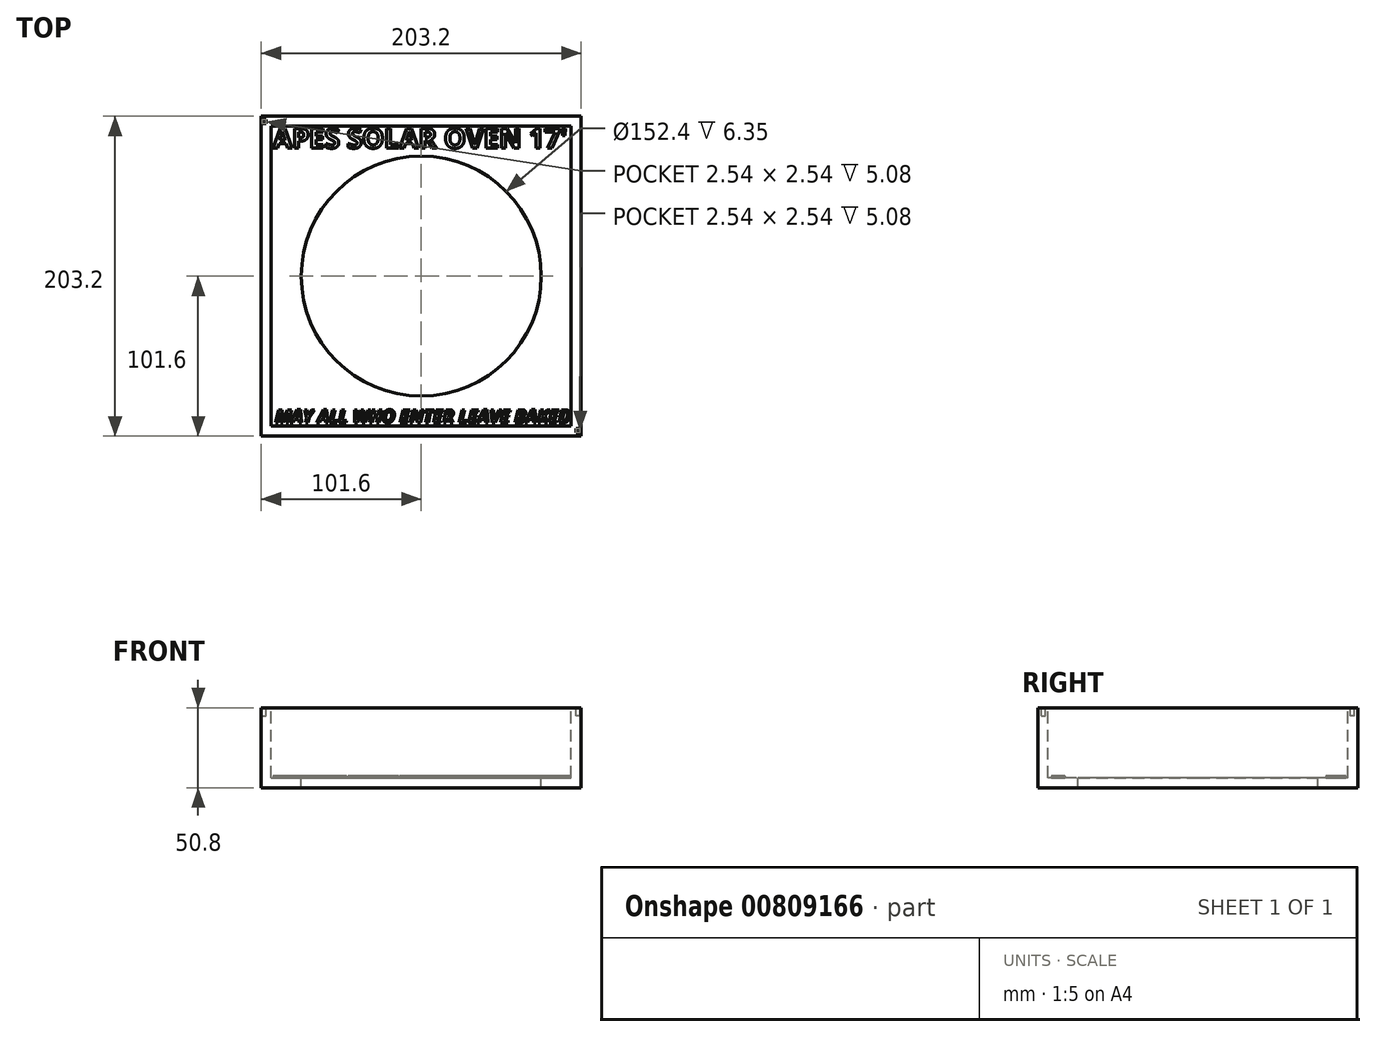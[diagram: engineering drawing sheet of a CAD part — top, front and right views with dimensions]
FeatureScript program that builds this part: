
annotation { "Feature Type Name" : "Feature", "Feature Type Description" : "" }
export const myFeature = defineFeature(function(context is Context, id is Id, definition is map)
    precondition{}
    {
        {
            var Q0;
            Q0=qCreatedBy(makeId("Top.planeOp"),FACE);
            var sketch = newSketch(context, id + "F0", { "sketchPlane" : qUnion([Q0])});
            skLineSegment(sketch, "E0.bottom", {"start": v(-101.6, 101.6) * mm, "end": v(101.6, 101.6) * mm});
            skLineSegment(sketch, "E0.top", {"start": v(-101.6, -101.6) * mm, "end": v(101.6, -101.6) * mm});
            skLineSegment(sketch, "E0.left", {"start": v(-101.6, 101.6) * mm, "end": v(-101.6, -101.6) * mm});
            skLineSegment(sketch, "E0.right", {"start": v(101.6, 101.6) * mm, "end": v(101.6, -101.6) * mm});
            skPoint(sketch, "E0.middle", {"position": v(0, 0) * mm});
            skSolve(sketch);
        }
        {
            var Q0;
            Q0=makeQuery(id+"F0.imprint","IMPRINT",FACE,{"disambiguationData":[TD([[makeQuery(id+"F0.imprint","IMPRINT",EDGE,{"derivedFrom":sQuery(id+"F0.wireOp",EDGE,"E0.bottom")}),-1.0]])]});
            extrude(context, id + "F1", {"entities" : qUnion([Q0]), "depth" : 50.8 * mm, "offsetDistance" : 25.4 * mm});
        }
        {
            var Q0;
            Q0=makeQuery(id+"F1.opExtrude","CAP_FACE",FACE,{"disambiguationData":[OSD([sQuery(id+"F0.wireOp",EDGE,"E0.bottom"),sQuery(id+"F0.wireOp",EDGE,"E0.top"),sQuery(id+"F0.wireOp",EDGE,"E0.left"),sQuery(id+"F0.wireOp",EDGE,"E0.right")])],"isStart":false});
            var sketch = newSketch(context, id + "F2", { "sketchPlane" : qUnion([Q0])});
            skLineSegment(sketch, "E1.bottom", {"start": v(-95.25, 95.25) * mm, "end": v(95.25, 95.25) * mm});
            skLineSegment(sketch, "E1.top", {"start": v(-95.25, -95.25) * mm, "end": v(95.25, -95.25) * mm});
            skLineSegment(sketch, "E1.left", {"start": v(-95.25, 95.25) * mm, "end": v(-95.25, -95.25) * mm});
            skLineSegment(sketch, "E1.right", {"start": v(95.25, 95.25) * mm, "end": v(95.25, -95.25) * mm});
            skPoint(sketch, "E1.middle", {"position": v(0, 0) * mm});
            skSolve(sketch);
        }
        {
            var Q0;
            Q0=makeQuery(id+"F2.imprint","IMPRINT",FACE,{"disambiguationData":[TD([[makeQuery(id+"F2.imprint","IMPRINT",EDGE,{"derivedFrom":sQuery(id+"F2.wireOp",EDGE,"E1.bottom")}),-1.0]])]});
            extrude(context, id + "F3", {"entities" : qUnion([Q0]), "operationType" : NewBodyOperationType.REMOVE, "oppositeDirection" : true, "depth" : 44.45 * mm, "offsetDistance" : 25.4 * mm});
        }
        {
            var Q0;
            Q0=makeQuery(id+"F3.boolean.opBoolean","COPY",FACE,{"derivedFrom":makeQuery(id+"F3.opExtrude","CAP_FACE",FACE,{"disambiguationData":[OSD([sQuery(id+"F2.wireOp",EDGE,"E1.bottom"),sQuery(id+"F2.wireOp",EDGE,"E1.top"),sQuery(id+"F2.wireOp",EDGE,"E1.left"),sQuery(id+"F2.wireOp",EDGE,"E1.right")])],"isStart":false})});
            var sketch = newSketch(context, id + "F4", { "sketchPlane" : qUnion([Q0])});
            skCircle(sketch, "E2", {"center": v(0, 0) * mm, "radius": 76.2 * mm});
            skSolve(sketch);
        }
        {
            var Q0;
            Q0 = qSketchRegion(id + "F4", true);
            extrude(context, id + "F5", {"entities" : qUnion([Q0]), "operationType" : NewBodyOperationType.REMOVE, "oppositeDirection" : true, "depth" : 6.6 * mm, "offsetDistance" : 25.4 * mm});
        }
        {
            var Q0;
            Q0=makeQuery(id+"F3.boolean.opBoolean","COPY",FACE,{"derivedFrom":makeQuery(id+"F3.opExtrude","CAP_FACE",FACE,{"disambiguationData":[OSD([sQuery(id+"F2.wireOp",EDGE,"E1.bottom"),sQuery(id+"F2.wireOp",EDGE,"E1.top"),sQuery(id+"F2.wireOp",EDGE,"E1.left"),sQuery(id+"F2.wireOp",EDGE,"E1.right")])],"isStart":false})});
            var sketch = newSketch(context, id + "F6", { "sketchPlane" : qUnion([Q0])});
            skText(sketch, "E3", { "text": "APES SOLAR OVEN 17\'", "fontName": "OpenSans-Bold.ttf"});
            const initialGuessF6  = {"E3": [-0.09416, 0.08132, 1, 0, 0.01259]};
            skSetInitialGuess(sketch, initialGuessF6);
            skSolve(sketch);
        }
        {
            var Q0;
            Q0 = qSketchRegion(id + "F6", true);
            extrude(context, id + "F7", {"entities" : qUnion([Q0]), "operationType" : NewBodyOperationType.ADD, "depth" : 1.27 * mm, "offsetDistance" : 25.4 * mm});
        }
        {
            var Q0;
            Q0=makeQuery(id+"F1.opExtrude","CAP_FACE",FACE,{"disambiguationData":[OSD([sQuery(id+"F0.wireOp",EDGE,"E0.bottom"),sQuery(id+"F0.wireOp",EDGE,"E0.top"),sQuery(id+"F0.wireOp",EDGE,"E0.left"),sQuery(id+"F0.wireOp",EDGE,"E0.right")])],"isStart":false});
            var sketch = newSketch(context, id + "F8", { "sketchPlane" : qUnion([Q0])});
            skLineSegment(sketch, "E4.bottom", {"start": v(-100.94, 99.36) * mm, "end": v(-98.4, 99.36) * mm});
            skLineSegment(sketch, "E4.top", {"start": v(-100.94, 96.82) * mm, "end": v(-98.4, 96.82) * mm});
            skLineSegment(sketch, "E4.left", {"start": v(-100.94, 99.36) * mm, "end": v(-100.94, 96.82) * mm});
            skLineSegment(sketch, "E4.right", {"start": v(-98.4, 99.36) * mm, "end": v(-98.4, 96.82) * mm});
            skSolve(sketch);
        }
        {
            var Q0;
            Q0 = qSketchRegion(id + "F8", true);
            extrude(context, id + "F9", {"entities" : qUnion([Q0]), "operationType" : NewBodyOperationType.REMOVE, "oppositeDirection" : true, "depth" : 5.08 * mm, "offsetDistance" : 25.4 * mm});
        }
        {
            var Q0;
            Q0=makeQuery(id+"F1.opExtrude","CAP_FACE",FACE,{"disambiguationData":[OSD([sQuery(id+"F0.wireOp",EDGE,"E0.bottom"),sQuery(id+"F0.wireOp",EDGE,"E0.top"),sQuery(id+"F0.wireOp",EDGE,"E0.left"),sQuery(id+"F0.wireOp",EDGE,"E0.right")])],"isStart":false});
            var sketch = newSketch(context, id + "F10", { "sketchPlane" : qUnion([Q0])});
            skLineSegment(sketch, "E5.bottom", {"start": v(100.94, -99.36) * mm, "end": v(98.4, -99.36) * mm});
            skLineSegment(sketch, "E5.top", {"start": v(100.94, -96.82) * mm, "end": v(98.4, -96.82) * mm});
            skLineSegment(sketch, "E5.left", {"start": v(100.94, -99.36) * mm, "end": v(100.94, -96.82) * mm});
            skLineSegment(sketch, "E5.right", {"start": v(98.4, -99.36) * mm, "end": v(98.4, -96.82) * mm});
            skSolve(sketch);
        }
        {
            var Q0;
            Q0 = qSketchRegion(id + "F10", true);
            extrude(context, id + "F11", {"entities" : qUnion([Q0]), "operationType" : NewBodyOperationType.REMOVE, "oppositeDirection" : true, "depth" : 5.08 * mm, "offsetDistance" : 25.4 * mm});
        }
        {
            var Q0;
            {var subQ0=sQuery(id+"F2.wireOp",EDGE,"E1.bottom");var subQ1=sQuery(id+"F2.wireOp",EDGE,"E1.top");var subQ2=sQuery(id+"F2.wireOp",EDGE,"E1.left");var subQ3=sQuery(id+"F2.wireOp",EDGE,"E1.right");Q0=makeQuery(id+"F7.boolean.opBoolean","SPLIT",FACE,{"disambiguationData":[TD([makeQuery(id+"F3.boolean.opBoolean","COPY",FACE,{"derivedFrom":makeQuery(id+"F3.opExtrude","SWEPT_FACE",FACE,{"disambiguationData":[OSD([subQ0])]})})])],"derivedFrom":makeQuery(id+"F3.boolean.opBoolean","COPY",FACE,{"derivedFrom":makeQuery(id+"F3.opExtrude","CAP_FACE",FACE,{"disambiguationData":[OSD([subQ0,subQ1,subQ2,subQ3])],"isStart":false})})});}
            var sketch = newSketch(context, id + "F12", { "sketchPlane" : qUnion([Q0])});
            skText(sketch, "E6", { "text": "MAY ALL WHO ENTER LEAVE BAKED", "fontName": "OpenSans-BoldItalic.ttf"});
            const initialGuessF12  = {"E6": [-0.0927, -0.0931, 1, 0, 0.00832]};
            skSetInitialGuess(sketch, initialGuessF12);
            skSolve(sketch);
        }
        {
            var Q0;
            Q0 = qSketchRegion(id + "F12", true);
            extrude(context, id + "F13", {"entities" : qUnion([Q0]), "operationType" : NewBodyOperationType.ADD, "depth" : 1.27 * mm, "offsetDistance" : 25.4 * mm});
        }
    });
